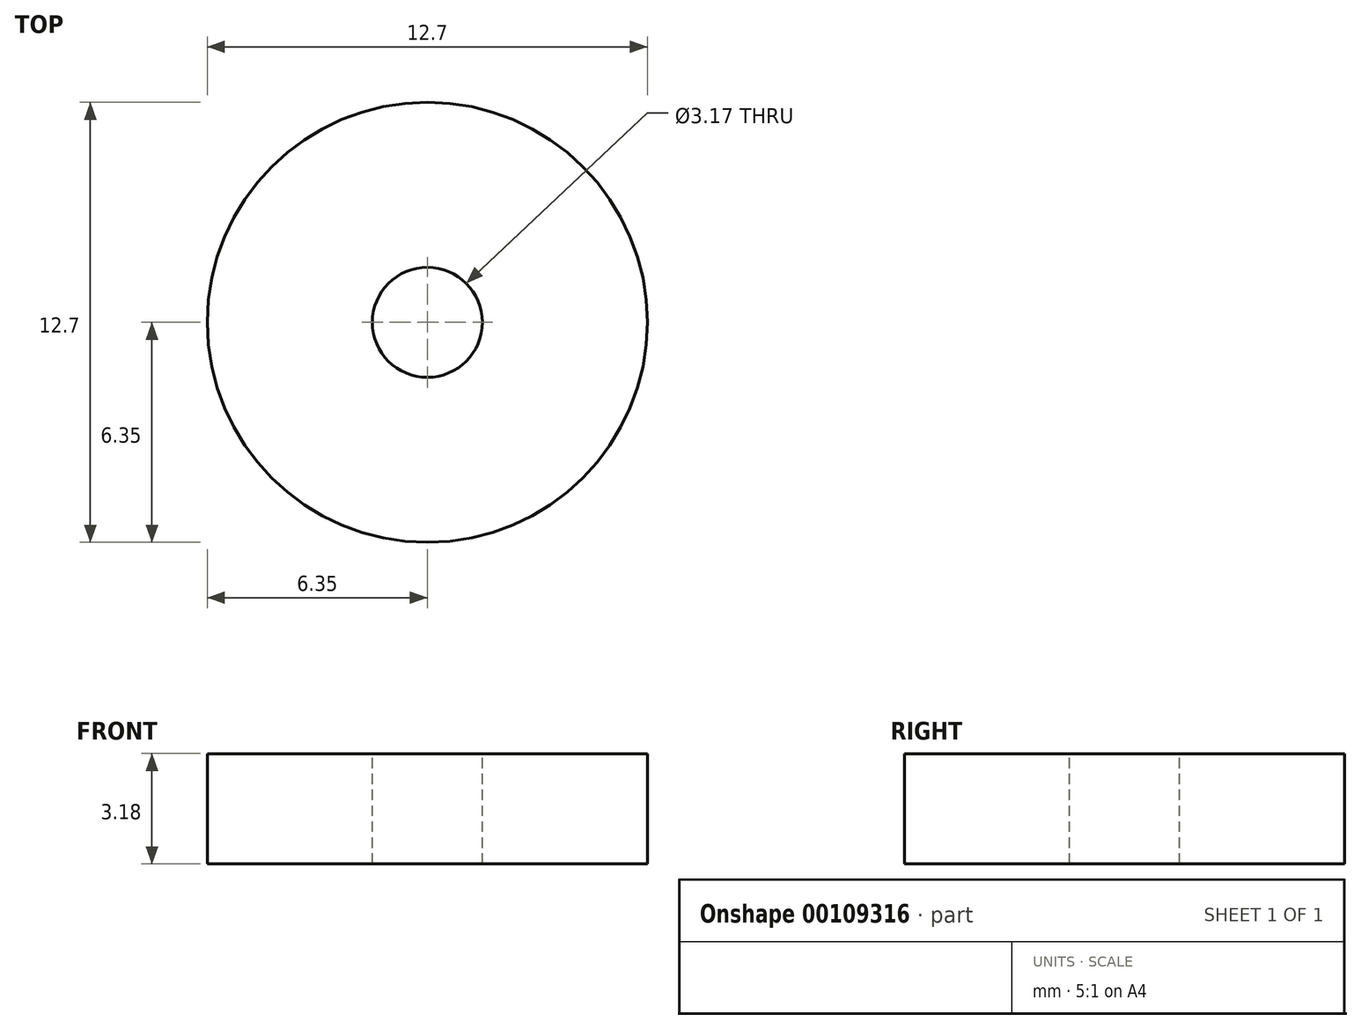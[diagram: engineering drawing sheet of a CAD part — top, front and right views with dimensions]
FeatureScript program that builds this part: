
annotation { "Feature Type Name" : "Feature", "Feature Type Description" : "" }
export const myFeature = defineFeature(function(context is Context, id is Id, definition is map)
    precondition{}
    {
        {
            var Q0;
            Q0=qCreatedBy(makeId("Top.planeOp"),FACE);
            var sketch = newSketch(context, id + "F0", { "sketchPlane" : qUnion([Q0])});
            skCircle(sketch, "E0", {"center": v(0, 0) * mm, "radius": 6.35 * mm});
            skSolve(sketch);
        }
        {
            var Q0;
            Q0=qSketchRegion(id+"F0",true);
            extrude(context, id + "F1", {"entities" : qUnion([Q0]), "depth" : 3.17 * mm});
        }
        {
            var Q0;
            Q0=makeQuery(id+"F1.opExtrude","CAP_FACE",FACE,{"disambiguationData":[OSD([sQuery(id+"F0.wireOp",EDGE,"E0")])],"isStart":false});
            var sketch = newSketch(context, id + "F2", { "sketchPlane" : qUnion([Q0])});
            skCircle(sketch, "E1", {"center": v(0, 0) * mm, "radius": 1.59 * mm});
            skSolve(sketch);
        }
        {
            var Q0;
            Q0=makeQuery(id+"F2.imprint","IMPRINT",FACE,{"disambiguationData":[TD([[makeQuery(id+"F2.imprint","IMPRINT",EDGE,{"derivedFrom":sQuery(id+"F2.wireOp",EDGE,"E1")}),1.0]])]});
            extrude(context, id + "F3", {"entities" : qUnion([Q0]), "operationType" : NewBodyOperationType.REMOVE, "endBound" : BoundingType.THROUGH_ALL, "oppositeDirection" : true, "depth" : 25.4 * mm});
        }
    });
